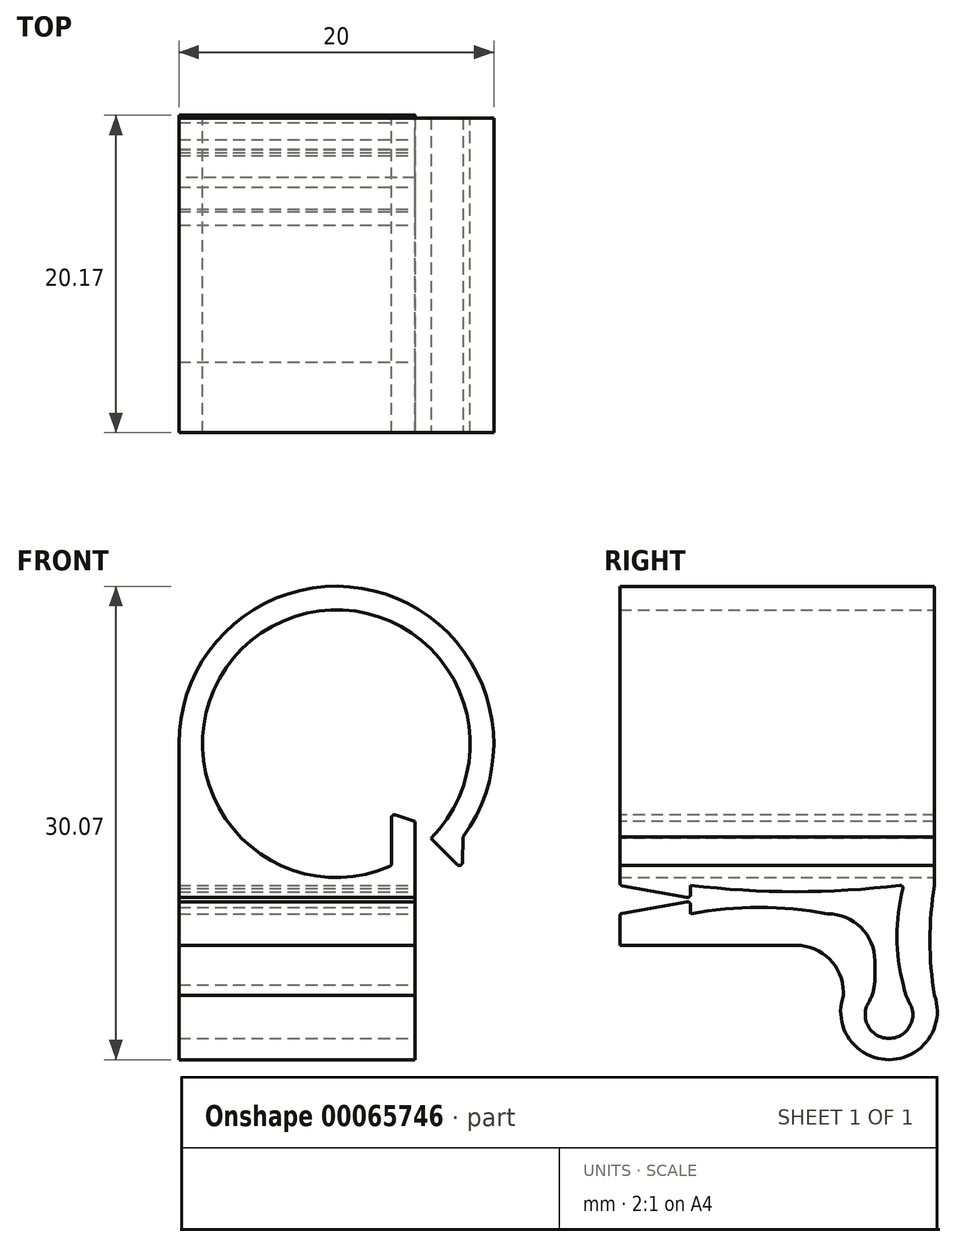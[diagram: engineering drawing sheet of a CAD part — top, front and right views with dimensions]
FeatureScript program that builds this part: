
annotation { "Feature Type Name" : "Feature", "Feature Type Description" : "" }
export const myFeature = defineFeature(function(context is Context, id is Id, definition is map)
    precondition{}
    {
        {
            var Q0;
            Q0=qCreatedBy(makeId("Front.planeOp"),FACE);
            var sketch = newSketch(context, id + "F0", { "sketchPlane" : qUnion([Q0])});
            skLineSegment(sketch, "E0", {"start": v(0, 0) * mm, "end": v(0, 18) * mm});
            skLineSegment(sketch, "E1", {"start": v(0, 0) * mm, "end": v(15, 0) * mm});
            skLineSegment(sketch, "E2", {"start": v(15, 0) * mm, "end": v(15, 18) * mm, "construction": true});
            skPoint(sketch, "E3", {"position": v(10, 18) * mm});
            skArc(sketch, "E4", {"start": v(0, 18) * mm, "mid": v(15, 26.66) * mm, "end": v(15, 9.34) * mm});
            skLineSegment(sketch, "E5", {"start": v(15, 9.34) * mm, "end": v(15, 0) * mm});
            skCircle(sketch, "E6", {"center": v(10, 18) * mm, "radius": 8.5 * mm});
            skSolve(sketch);
        }
        {
            var Q0;
            Q0=makeQuery(id+"F0.imprint","IMPRINT",FACE,{"disambiguationData":[TD([[makeQuery(id+"F0.imprint","IMPRINT",EDGE,{"derivedFrom":sQuery(id+"F0.wireOp",EDGE,"E0")}),-1.0]])]});
            extrude(context, id + "F1", {"entities" : qUnion([Q0]), "depth" : 20 * mm});
        }
        {
            var Q0;
            Q0=makeQuery(id+"F1.opExtrude","SWEPT_FACE",FACE,{"disambiguationData":[OSD([sQuery(id+"F0.wireOp",EDGE,"E5")])]});
            var sketch = newSketch(context, id + "F2", { "sketchPlane" : qUnion([Q0])});
            skLineSegment(sketch, "E7", {"start": v(-2, 2) * mm, "end": v(-2, 9) * mm});
            skLineSegment(sketch, "E8", {"start": v(-2, 9) * mm, "end": v(-20, 9) * mm});
            skLineSegment(sketch, "E9", {"start": v(-2, 2) * mm, "end": v(-3.8, 2) * mm});
            skLineSegment(sketch, "E10", {"start": v(-3.8, 2) * mm, "end": v(-3.8, 7.2) * mm});
            skLineSegment(sketch, "E11", {"start": v(-3.8, 7.2) * mm, "end": v(-20, 7.2) * mm});
            skLineSegment(sketch, "E12", {"start": v(-20, 9) * mm, "end": v(-20, 7.2) * mm});
            skLineSegment(sketch, "E13.bottom", {"start": v(-20, 0) * mm, "end": v(-5.8, 0) * mm});
            skLineSegment(sketch, "E13.top", {"start": v(-20, 5.2) * mm, "end": v(-5.8, 5.2) * mm});
            skLineSegment(sketch, "E13.left", {"start": v(-20, 0) * mm, "end": v(-20, 5.2) * mm});
            skLineSegment(sketch, "E13.right", {"start": v(-5.8, 0) * mm, "end": v(-5.8, 5.2) * mm});
            skSolve(sketch);
        }
        {
            var Q0;
            Q0 = qSketchRegion(id + "F2", true);
            extrude(context, id + "F3", {"entities" : qUnion([Q0]), "operationType" : NewBodyOperationType.REMOVE, "endBound" : BoundingType.THROUGH_ALL, "oppositeDirection" : true, "depth" : 25 * mm});
        }
        {
            var Q0;
            Q0=makeQuery(id+"F1.opExtrude","SWEPT_FACE",FACE,{"disambiguationData":[OSD([sQuery(id+"F0.wireOp",EDGE,"E5")])]});
            var sketch = newSketch(context, id + "F4", { "sketchPlane" : qUnion([Q0])});
            skLineSegment(sketch, "E14", {"start": v(-15.5, 7.2) * mm, "end": v(-15.5, 8) * mm});
            skLineSegment(sketch, "E15", {"start": v(-15.5, 8) * mm, "end": v(-20, 7.2) * mm});
            skLineSegment(sketch, "E16", {"start": v(-20, 7.2) * mm, "end": v(-15.5, 7.2) * mm});
            skLineSegment(sketch, "E17", {"start": v(-15.5, 9) * mm, "end": v(-15.5, 8.2) * mm});
            skLineSegment(sketch, "E18", {"start": v(-15.5, 8.2) * mm, "end": v(-20, 9) * mm});
            skLineSegment(sketch, "E19", {"start": v(-20, 9) * mm, "end": v(-15.5, 9) * mm});
            skSolve(sketch);
        }
        {
            var Q0;
            Q0 = qSketchRegion(id + "F4", true);
            var Q1;
            Q1=makeQuery(id+"F1.opExtrude","SWEPT_FACE",FACE,{"disambiguationData":[OSD([sQuery(id+"F0.wireOp",EDGE,"E0")])]});
            extrude(context, id + "F5", {"entities" : qUnion([Q0]), "operationType" : NewBodyOperationType.ADD, "endBound" : BoundingType.UP_TO_SURFACE, "oppositeDirection" : true, "endBoundEntityFace" : qUnion([Q1]), "depth" : 25 * mm});
        }
        {
            var Q0;
            {var subQ0=sQuery(id+"F0.wireOp",EDGE,"E6");var subQ1=sQuery(id+"F0.wireOp",EDGE,"E5");var subQ2=sQuery(id+"F0.wireOp",EDGE,"E4");var subQ3=sQuery(id+"F0.wireOp",EDGE,"E0");Q0=makeQuery(id+"F3.boolean.opBoolean","SPLIT",FACE,{"disambiguationData":[TD([makeQuery(id+"F1.opExtrude","SWEPT_FACE",FACE,{"disambiguationData":[OSD([subQ2])]})])],"derivedFrom":makeQuery(id+"F1.opExtrude","CAP_FACE",FACE,{"disambiguationData":[OSD([subQ3,sQuery(id+"F0.wireOp",EDGE,"E1"),subQ2,subQ1,subQ0])],"isStart":false})});}
            var sketch = newSketch(context, id + "F6", { "sketchPlane" : qUnion([Q0])});
            skLineSegment(sketch, "E20.bottom", {"start": v(15, 9.34) * mm, "end": v(16, 9.34) * mm});
            skLineSegment(sketch, "E20.top", {"start": v(15, 11.98) * mm, "end": v(16, 11.98) * mm});
            skLineSegment(sketch, "E20.left", {"start": v(15, 9.34) * mm, "end": v(15, 11.98) * mm});
            skLineSegment(sketch, "E20.right", {"start": v(16, 9.34) * mm, "end": v(16, 11.98) * mm});
            skSolve(sketch);
        }
        {
            var Q0;
            Q0 = qSketchRegion(id + "F6", true);
            extrude(context, id + "F7", {"entities" : qUnion([Q0]), "operationType" : NewBodyOperationType.REMOVE, "endBound" : BoundingType.THROUGH_ALL, "oppositeDirection" : true, "depth" : 25 * mm});
        }
        {
            var Q0;
            {var subQ0=sQuery(id+"F0.wireOp",EDGE,"E6");var subQ1=sQuery(id+"F0.wireOp",EDGE,"E5");var subQ2=sQuery(id+"F0.wireOp",EDGE,"E4");var subQ3=sQuery(id+"F0.wireOp",EDGE,"E0");Q0=makeQuery(id+"F3.boolean.opBoolean","SPLIT",FACE,{"disambiguationData":[TD([makeQuery(id+"F1.opExtrude","SWEPT_FACE",FACE,{"disambiguationData":[OSD([subQ2])]})])],"derivedFrom":makeQuery(id+"F1.opExtrude","CAP_FACE",FACE,{"disambiguationData":[OSD([subQ3,sQuery(id+"F0.wireOp",EDGE,"E1"),subQ2,subQ1,subQ0])],"isStart":false})});}
            var sketch = newSketch(context, id + "F8", { "sketchPlane" : qUnion([Q0])});
            skLineSegment(sketch, "E21.bottom", {"start": v(15, 10.06) * mm, "end": v(13.5, 10.06) * mm});
            skLineSegment(sketch, "E21.top", {"start": v(15, 13.56) * mm, "end": v(13.5, 13.56) * mm});
            skLineSegment(sketch, "E21.left", {"start": v(15, 10.06) * mm, "end": v(15, 13.56) * mm});
            skLineSegment(sketch, "E21.right", {"start": v(13.5, 10.06) * mm, "end": v(13.5, 13.56) * mm});
            skLineSegment(sketch, "E22", {"start": v(16, 11.98) * mm, "end": v(18, 10) * mm});
            skLineSegment(sketch, "E23", {"start": v(18, 10) * mm, "end": v(18.05, 12.06) * mm});
            skLineSegment(sketch, "E24", {"start": v(18.05, 12.06) * mm, "end": v(16, 11.98) * mm});
            skSolve(sketch);
        }
        {
            var Q0;
            Q0 = qSketchRegion(id + "F8", true);
            var Q1;
            Q1=makeQuery(id+"F1.opExtrude","CAP_FACE",FACE,{"disambiguationData":[OSD([sQuery(id+"F0.wireOp",EDGE,"E0"),sQuery(id+"F0.wireOp",EDGE,"E1"),sQuery(id+"F0.wireOp",EDGE,"E4"),sQuery(id+"F0.wireOp",EDGE,"E5"),sQuery(id+"F0.wireOp",EDGE,"E6")])],"isStart":true});
            extrude(context, id + "F9", {"entities" : qUnion([Q0]), "operationType" : NewBodyOperationType.ADD, "endBound" : BoundingType.UP_TO_SURFACE, "oppositeDirection" : true, "endBoundEntityFace" : qUnion([Q1]), "depth" : 25 * mm});
        }
        {
            var Q0;
            {var subQ0=sQuery(id+"F0.wireOp",EDGE,"E6");var subQ1=sQuery(id+"F0.wireOp",EDGE,"E5");var subQ2=sQuery(id+"F0.wireOp",EDGE,"E4");var subQ3=sQuery(id+"F0.wireOp",EDGE,"E0");Q0=makeQuery(id+"F9.boolean.opBoolean","MERGE",FACE,{"derivedFrom":[makeQuery(id+"F3.boolean.opBoolean","SPLIT",FACE,{"disambiguationData":[TD([makeQuery(id+"F1.opExtrude","SWEPT_FACE",FACE,{"disambiguationData":[OSD([subQ2])]})])],"derivedFrom":makeQuery(id+"F1.opExtrude","CAP_FACE",FACE,{"disambiguationData":[OSD([subQ3,sQuery(id+"F0.wireOp",EDGE,"E1"),subQ2,subQ1,subQ0])],"isStart":false})}),makeQuery(id+"F9.opExtrude","CAP_FACE",FACE,{"disambiguationData":[OSD([sQuery(id+"F8.wireOp",EDGE,"E21.bottom"),sQuery(id+"F8.wireOp",EDGE,"E21.top"),sQuery(id+"F8.wireOp",EDGE,"E21.left"),sQuery(id+"F8.wireOp",EDGE,"E21.right")])],"isStart":true}),makeQuery(id+"F9.opExtrude","CAP_FACE",FACE,{"disambiguationData":[OSD([sQuery(id+"F8.wireOp",EDGE,"E22"),sQuery(id+"F8.wireOp",EDGE,"E23"),sQuery(id+"F8.wireOp",EDGE,"E24")])],"isStart":true})]});}
            var sketch = newSketch(context, id + "F10", { "sketchPlane" : qUnion([Q0])});
            skLineSegment(sketch, "E25", {"start": v(16, 10) * mm, "end": v(16, 11.98) * mm});
            skLineSegment(sketch, "E26", {"start": v(17.07, 10.92) * mm, "end": v(16, 11.98) * mm});
            skLineSegment(sketch, "E27", {"start": v(13.5, 13.56) * mm, "end": v(15, 13.06) * mm});
            skLineSegment(sketch, "E28", {"start": v(15, 13.06) * mm, "end": v(15, 13.56) * mm});
            skLineSegment(sketch, "E29", {"start": v(15, 13.56) * mm, "end": v(13.5, 13.56) * mm});
            skLineSegment(sketch, "E30", {"start": v(16, 10) * mm, "end": v(17.07, 10) * mm});
            skLineSegment(sketch, "E31", {"start": v(17.07, 10) * mm, "end": v(17.07, 10.92) * mm});
            skSolve(sketch);
        }
        {
            var Q0;
            Q0 = qSketchRegion(id + "F10", true);
            var Q1;
            Q1=makeQuery(id+"F9.boolean.opBoolean","MERGE",FACE,{"derivedFrom":[makeQuery(id+"F1.opExtrude","CAP_FACE",FACE,{"disambiguationData":[OSD([sQuery(id+"F0.wireOp",EDGE,"E0"),sQuery(id+"F0.wireOp",EDGE,"E1"),sQuery(id+"F0.wireOp",EDGE,"E4"),sQuery(id+"F0.wireOp",EDGE,"E5"),sQuery(id+"F0.wireOp",EDGE,"E6")])],"isStart":true}),makeQuery(id+"F9.opExtrude","CAP_FACE",FACE,{"disambiguationData":[OSD([sQuery(id+"F8.wireOp",EDGE,"E21.bottom"),sQuery(id+"F8.wireOp",EDGE,"E21.top"),sQuery(id+"F8.wireOp",EDGE,"E21.left"),sQuery(id+"F8.wireOp",EDGE,"E21.right")])],"isStart":false}),makeQuery(id+"F9.opExtrude","CAP_FACE",FACE,{"disambiguationData":[OSD([sQuery(id+"F8.wireOp",EDGE,"E22"),sQuery(id+"F8.wireOp",EDGE,"E23"),sQuery(id+"F8.wireOp",EDGE,"E24")])],"isStart":false})]});
            extrude(context, id + "F11", {"entities" : qUnion([Q0]), "operationType" : NewBodyOperationType.REMOVE, "endBound" : BoundingType.UP_TO_SURFACE, "oppositeDirection" : true, "endBoundEntityFace" : qUnion([Q1]), "depth" : 25 * mm});
        }
        {
            var Q0;
            Q0=makeQuery(id+"F9.boolean.opBoolean","MERGE",FACE,{"derivedFrom":[makeQuery(id+"F7.boolean.opBoolean","MERGE",FACE,{"derivedFrom":[makeQuery(id+"F5.boolean.opBoolean","MERGE",FACE,{"derivedFrom":[makeQuery(id+"F1.opExtrude","SWEPT_FACE",FACE,{"disambiguationData":[OSD([sQuery(id+"F0.wireOp",EDGE,"E5")])]}),makeQuery(id+"F5.opExtrude","CAP_FACE",FACE,{"disambiguationData":[OSD([sQuery(id+"F4.wireOp",EDGE,"E14"),sQuery(id+"F4.wireOp",EDGE,"E15"),sQuery(id+"F4.wireOp",EDGE,"E16")])],"isStart":true}),makeQuery(id+"F5.opExtrude","CAP_FACE",FACE,{"disambiguationData":[OSD([sQuery(id+"F4.wireOp",EDGE,"E17"),sQuery(id+"F4.wireOp",EDGE,"E18"),sQuery(id+"F4.wireOp",EDGE,"E19")])],"isStart":true})]}),makeQuery(id+"F7.opExtrude","SWEPT_FACE",FACE,{"disambiguationData":[OSD([sQuery(id+"F6.wireOp",EDGE,"E20.left")])]})]}),makeQuery(id+"F9.opExtrude","SWEPT_FACE",FACE,{"disambiguationData":[OSD([sQuery(id+"F8.wireOp",EDGE,"E21.left")])]})]});
            var sketch = newSketch(context, id + "F12", { "sketchPlane" : qUnion([Q0])});
            skArc(sketch, "E32", {"start": v(-5.8, 2) * mm, "mid": v(-2.9, -2.07) * mm, "end": v(0, 2) * mm});
            skLineSegment(sketch, "E33", {"start": v(-5.8, 2) * mm, "end": v(0, 2) * mm});
            skSolve(sketch);
        }
        {
            var Q0;
            Q0 = qSketchRegion(id + "F12", true);
            var Q1;
            Q1=makeQuery(id+"F5.boolean.opBoolean","MERGE",FACE,{"derivedFrom":[makeQuery(id+"F1.opExtrude","SWEPT_FACE",FACE,{"disambiguationData":[OSD([sQuery(id+"F0.wireOp",EDGE,"E0")])]}),makeQuery(id+"F5.opExtrude","CAP_FACE",FACE,{"disambiguationData":[OSD([sQuery(id+"F4.wireOp",EDGE,"E14"),sQuery(id+"F4.wireOp",EDGE,"E15"),sQuery(id+"F4.wireOp",EDGE,"E16")])],"isStart":false}),makeQuery(id+"F5.opExtrude","CAP_FACE",FACE,{"disambiguationData":[OSD([sQuery(id+"F4.wireOp",EDGE,"E17"),sQuery(id+"F4.wireOp",EDGE,"E18"),sQuery(id+"F4.wireOp",EDGE,"E19")])],"isStart":false})]});
            extrude(context, id + "F13", {"entities" : qUnion([Q0]), "operationType" : NewBodyOperationType.ADD, "endBound" : BoundingType.UP_TO_SURFACE, "oppositeDirection" : true, "endBoundEntityFace" : qUnion([Q1]), "depth" : 25 * mm});
        }
        {
            var Q0;
            Q0=makeQuery(id+"F13.boolean.opBoolean","MERGE",FACE,{"derivedFrom":[makeQuery(id+"F9.boolean.opBoolean","MERGE",FACE,{"derivedFrom":[makeQuery(id+"F7.boolean.opBoolean","MERGE",FACE,{"derivedFrom":[makeQuery(id+"F5.boolean.opBoolean","MERGE",FACE,{"derivedFrom":[makeQuery(id+"F1.opExtrude","SWEPT_FACE",FACE,{"disambiguationData":[OSD([sQuery(id+"F0.wireOp",EDGE,"E5")])]}),makeQuery(id+"F5.opExtrude","CAP_FACE",FACE,{"disambiguationData":[OSD([sQuery(id+"F4.wireOp",EDGE,"E14"),sQuery(id+"F4.wireOp",EDGE,"E15"),sQuery(id+"F4.wireOp",EDGE,"E16")])],"isStart":true}),makeQuery(id+"F5.opExtrude","CAP_FACE",FACE,{"disambiguationData":[OSD([sQuery(id+"F4.wireOp",EDGE,"E17"),sQuery(id+"F4.wireOp",EDGE,"E18"),sQuery(id+"F4.wireOp",EDGE,"E19")])],"isStart":true})]}),makeQuery(id+"F7.opExtrude","SWEPT_FACE",FACE,{"disambiguationData":[OSD([sQuery(id+"F6.wireOp",EDGE,"E20.left")])]})]}),makeQuery(id+"F9.opExtrude","SWEPT_FACE",FACE,{"disambiguationData":[OSD([sQuery(id+"F8.wireOp",EDGE,"E21.left")])]})]}),makeQuery(id+"F13.opExtrude","CAP_FACE",FACE,{"disambiguationData":[OSD([sQuery(id+"F12.wireOp",EDGE,"E32"),sQuery(id+"F12.wireOp",EDGE,"E33")])],"isStart":true})]});
            var sketch = newSketch(context, id + "F14", { "sketchPlane" : qUnion([Q0])});
            skArc(sketch, "E34", {"start": v(-3.8, 2) * mm, "mid": v(-2.9, -0.72) * mm, "end": v(-2, 2) * mm});
            skLineSegment(sketch, "E35", {"start": v(-3.8, 2) * mm, "end": v(-2, 2) * mm});
            skArc(sketch, "E36", {"start": v(0, 9) * mm, "mid": v(-0.3, 5.5) * mm, "end": v(0, 2) * mm});
            skLineSegment(sketch, "E37", {"start": v(0, 2) * mm, "end": v(0, 9) * mm});
            skSolve(sketch);
        }
        {
            var Q0;
            Q0 = qSketchRegion(id + "F14", true);
            extrude(context, id + "F15", {"entities" : qUnion([Q0]), "operationType" : NewBodyOperationType.REMOVE, "endBound" : BoundingType.THROUGH_ALL, "oppositeDirection" : true, "depth" : 25 * mm});
        }
        {
            var Q0;
            Q0=makeQuery(id+"F3.boolean.opBoolean","COPY",EDGE,{"derivedFrom":makeQuery(id+"F3.opExtrude","SWEPT_EDGE",EDGE,{"disambiguationData":[OSD([sQuery(id+"F2.wireOp",EDGE,"E10"),sQuery(id+"F2.wireOp",EDGE,"E11")])]})});
            var Q1;
            Q1=makeQuery(id+"F3.boolean.opBoolean","COPY",EDGE,{"derivedFrom":makeQuery(id+"F3.opExtrude","SWEPT_EDGE",EDGE,{"disambiguationData":[OSD([sQuery(id+"F2.wireOp",EDGE,"E13.top"),sQuery(id+"F2.wireOp",EDGE,"E13.right")])]})});
            var Q2;
            {var subQ0=sQuery(id+"F2.wireOp",EDGE,"E10");Q2=makeQuery(id+"F15.boolean.opBoolean","MERGE",EDGE,{"derivedFrom":[makeQuery(id+"F3.boolean.opBoolean","COPY",EDGE,{"derivedFrom":makeQuery(id+"F3.opExtrude","SWEPT_EDGE",EDGE,{"disambiguationData":[OSD([sQuery(id+"F2.wireOp",EDGE,"E9"),subQ0])]})}),makeQuery(id+"F15.opExtrude","SWEPT_EDGE",EDGE,{"disambiguationData":[OSD([subQ0,sQuery(id+"F14.wireOp",EDGE,"E34"),sQuery(id+"F14.wireOp",EDGE,"E35")])]})]});}
            var Q3;
            {var subQ0=sQuery(id+"F2.wireOp",EDGE,"E7");Q3=makeQuery(id+"F15.boolean.opBoolean","MERGE",EDGE,{"derivedFrom":[makeQuery(id+"F3.boolean.opBoolean","COPY",EDGE,{"derivedFrom":makeQuery(id+"F3.opExtrude","SWEPT_EDGE",EDGE,{"disambiguationData":[OSD([subQ0,sQuery(id+"F2.wireOp",EDGE,"E9")])]})}),makeQuery(id+"F15.opExtrude","SWEPT_EDGE",EDGE,{"disambiguationData":[OSD([subQ0,sQuery(id+"F14.wireOp",EDGE,"E34"),sQuery(id+"F14.wireOp",EDGE,"E35")])]})]});}
            var Q4;
            Q4=makeQuery(id+"F15.boolean.opBoolean","COPY",EDGE,{"derivedFrom":makeQuery(id+"F15.opExtrude","SWEPT_EDGE",EDGE,{"disambiguationData":[OSD([sQuery(id+"F0.wireOp",EDGE,"E0"),sQuery(id+"F0.wireOp",EDGE,"E1"),sQuery(id+"F0.wireOp",EDGE,"E4"),sQuery(id+"F0.wireOp",EDGE,"E5"),sQuery(id+"F0.wireOp",EDGE,"E6"),sQuery(id+"F6.wireOp",EDGE,"E20.left"),sQuery(id+"F8.wireOp",EDGE,"E21.left"),sQuery(id+"F14.wireOp",EDGE,"E36"),sQuery(id+"F14.wireOp",EDGE,"E37")])]})});
            var Q5;
            {var subQ0=sQuery(id+"F12.wireOp",EDGE,"E32");Q5=makeQuery(id+"F15.boolean.opBoolean","MERGE",EDGE,{"derivedFrom":[makeQuery(id+"F13.opExtrude","SWEPT_EDGE",EDGE,{"disambiguationData":[OSD([sQuery(id+"F0.wireOp",EDGE,"E0"),sQuery(id+"F0.wireOp",EDGE,"E1"),sQuery(id+"F0.wireOp",EDGE,"E4"),sQuery(id+"F0.wireOp",EDGE,"E5"),sQuery(id+"F0.wireOp",EDGE,"E6"),sQuery(id+"F6.wireOp",EDGE,"E20.left"),sQuery(id+"F8.wireOp",EDGE,"E21.left"),subQ0,sQuery(id+"F12.wireOp",EDGE,"E33")])]}),makeQuery(id+"F15.opExtrude","SWEPT_EDGE",EDGE,{"disambiguationData":[OSD([subQ0,sQuery(id+"F14.wireOp",EDGE,"E36"),sQuery(id+"F14.wireOp",EDGE,"E37")])]})]});}
            fillet(context, id + "F16", {"entities" : qUnion([Q0, Q1, Q2, Q3, Q4, Q5]), "radius" : 3 * mm, "tangentPropagation" : true, "allowEdgeOverflow" : false});
        }
        {
            var Q0;
            {var subQ0=sQuery(id+"F0.wireOp",EDGE,"E5");Q0=makeQuery(id+"F5.boolean.opBoolean","MERGE",EDGE,{"derivedFrom":[makeQuery(id+"F3.boolean.opBoolean","COPY",EDGE,{"derivedFrom":makeQuery(id+"F3.opExtrude","SWEPT_EDGE",EDGE,{"disambiguationData":[OSD([subQ0,sQuery(id+"F2.wireOp",EDGE,"E11"),sQuery(id+"F2.wireOp",EDGE,"E12")])]})}),makeQuery(id+"F5.opExtrude","SWEPT_EDGE",EDGE,{"disambiguationData":[OSD([subQ0,sQuery(id+"F4.wireOp",EDGE,"E15"),sQuery(id+"F4.wireOp",EDGE,"E16")])]})]});}
            var Q1;
            {var subQ0=sQuery(id+"F0.wireOp",EDGE,"E5");Q1=makeQuery(id+"F5.boolean.opBoolean","MERGE",EDGE,{"derivedFrom":[makeQuery(id+"F3.boolean.opBoolean","COPY",EDGE,{"derivedFrom":makeQuery(id+"F3.opExtrude","SWEPT_EDGE",EDGE,{"disambiguationData":[OSD([subQ0,sQuery(id+"F2.wireOp",EDGE,"E8"),sQuery(id+"F2.wireOp",EDGE,"E12")])]})}),makeQuery(id+"F5.opExtrude","SWEPT_EDGE",EDGE,{"disambiguationData":[OSD([subQ0,sQuery(id+"F4.wireOp",EDGE,"E18"),sQuery(id+"F4.wireOp",EDGE,"E19")])]})]});}
            var Q2;
            Q2=makeQuery(id+"F5.opExtrude","SWEPT_EDGE",EDGE,{"disambiguationData":[OSD([sQuery(id+"F4.wireOp",EDGE,"E17"),sQuery(id+"F4.wireOp",EDGE,"E18")])]});
            var Q3;
            Q3=makeQuery(id+"F5.opExtrude","SWEPT_EDGE",EDGE,{"disambiguationData":[OSD([sQuery(id+"F4.wireOp",EDGE,"E14"),sQuery(id+"F4.wireOp",EDGE,"E15")])]});
            var Q4;
            Q4=makeQuery(id+"F3.boolean.opBoolean","COPY",EDGE,{"derivedFrom":makeQuery(id+"F3.opExtrude","SWEPT_EDGE",EDGE,{"disambiguationData":[OSD([sQuery(id+"F2.wireOp",EDGE,"E7"),sQuery(id+"F2.wireOp",EDGE,"E8")])]})});
            var Q5;
            Q5=makeQuery(id+"F9.opExtrude","SWEPT_EDGE",EDGE,{"disambiguationData":[OSD([sQuery(id+"F8.wireOp",EDGE,"E22"),sQuery(id+"F8.wireOp",EDGE,"E23")])]});
            var Q6;
            {var subQ0=sQuery(id+"F0.wireOp",EDGE,"E6");Q6=makeQuery(id+"F11.boolean.opBoolean","MERGE",EDGE,{"derivedFrom":[makeQuery(id+"F7.boolean.opBoolean","COPY",EDGE,{"derivedFrom":makeQuery(id+"F7.opExtrude","SWEPT_EDGE",EDGE,{"disambiguationData":[OSD([subQ0,sQuery(id+"F6.wireOp",EDGE,"E20.top"),sQuery(id+"F6.wireOp",EDGE,"E20.right")])]})}),makeQuery(id+"F11.opExtrude","SWEPT_EDGE",EDGE,{"disambiguationData":[OSD([subQ0,sQuery(id+"F10.wireOp",EDGE,"E25"),sQuery(id+"F10.wireOp",EDGE,"E26")])]})]});}
            var Q7;
            {var subQ0=sQuery(id+"F8.wireOp",EDGE,"E21.right");Q7=makeQuery(id+"F11.boolean.opBoolean","MERGE",EDGE,{"derivedFrom":[makeQuery(id+"F9.opExtrude","SWEPT_EDGE",EDGE,{"disambiguationData":[OSD([sQuery(id+"F8.wireOp",EDGE,"E21.top"),subQ0])]}),makeQuery(id+"F11.opExtrude","SWEPT_EDGE",EDGE,{"disambiguationData":[OSD([subQ0,sQuery(id+"F10.wireOp",EDGE,"E27"),sQuery(id+"F10.wireOp",EDGE,"E29")])]})]});}
            var Q8;
            Q8=makeQuery(id+"F11.boolean.opBoolean","COPY",EDGE,{"derivedFrom":makeQuery(id+"F11.opExtrude","SWEPT_EDGE",EDGE,{"disambiguationData":[OSD([sQuery(id+"F0.wireOp",EDGE,"E5"),sQuery(id+"F6.wireOp",EDGE,"E20.left"),sQuery(id+"F8.wireOp",EDGE,"E21.left"),sQuery(id+"F10.wireOp",EDGE,"E27"),sQuery(id+"F10.wireOp",EDGE,"E28")])]})});
            var Q9;
            Q9=makeQuery(id+"F9.boolean.opBoolean","INTERSECT",EDGE,{"derivedFrom":[makeQuery(id+"F1.opExtrude","SWEPT_FACE",FACE,{"disambiguationData":[OSD([sQuery(id+"F0.wireOp",EDGE,"E6")])]}),makeQuery(id+"F9.opExtrude","SWEPT_FACE",FACE,{"disambiguationData":[OSD([sQuery(id+"F8.wireOp",EDGE,"E21.right")])]})]});
            fillet(context, id + "F17", {"entities" : qUnion([Q0, Q1, Q2, Q3, Q4, Q5, Q6, Q7, Q8, Q9]), "radius" : 0.2 * mm, "tangentPropagation" : true, "allowEdgeOverflow" : false});
        }
        {
            var Q0;
            Q0=makeQuery(id+"F13.boolean.opBoolean","MERGE",FACE,{"derivedFrom":[makeQuery(id+"F9.boolean.opBoolean","MERGE",FACE,{"derivedFrom":[makeQuery(id+"F7.boolean.opBoolean","MERGE",FACE,{"derivedFrom":[makeQuery(id+"F5.boolean.opBoolean","MERGE",FACE,{"derivedFrom":[makeQuery(id+"F1.opExtrude","SWEPT_FACE",FACE,{"disambiguationData":[OSD([sQuery(id+"F0.wireOp",EDGE,"E5")])]}),makeQuery(id+"F5.opExtrude","CAP_FACE",FACE,{"disambiguationData":[OSD([sQuery(id+"F4.wireOp",EDGE,"E14"),sQuery(id+"F4.wireOp",EDGE,"E15"),sQuery(id+"F4.wireOp",EDGE,"E16")])],"isStart":true}),makeQuery(id+"F5.opExtrude","CAP_FACE",FACE,{"disambiguationData":[OSD([sQuery(id+"F4.wireOp",EDGE,"E17"),sQuery(id+"F4.wireOp",EDGE,"E18"),sQuery(id+"F4.wireOp",EDGE,"E19")])],"isStart":true})]}),makeQuery(id+"F7.opExtrude","SWEPT_FACE",FACE,{"disambiguationData":[OSD([sQuery(id+"F6.wireOp",EDGE,"E20.left")])]})]}),makeQuery(id+"F9.opExtrude","SWEPT_FACE",FACE,{"disambiguationData":[OSD([sQuery(id+"F8.wireOp",EDGE,"E21.left")])]})]}),makeQuery(id+"F13.opExtrude","CAP_FACE",FACE,{"disambiguationData":[OSD([sQuery(id+"F12.wireOp",EDGE,"E32"),sQuery(id+"F12.wireOp",EDGE,"E33")])],"isStart":true})]});
            var sketch = newSketch(context, id + "F18", { "sketchPlane" : qUnion([Q0])});
            skArc(sketch, "E38", {"start": v(-15.5, 9) * mm, "mid": v(-8.85, 8.6) * mm, "end": v(-2.2, 9) * mm});
            skLineSegment(sketch, "E39", {"start": v(-15.5, 9) * mm, "end": v(-2.2, 9) * mm});
            skArc(sketch, "E40", {"start": v(-6.8, 7.2) * mm, "mid": v(-11.15, 7.6) * mm, "end": v(-15.5, 7.2) * mm});
            skLineSegment(sketch, "E41", {"start": v(-15.5, 7.2) * mm, "end": v(-6.8, 7.2) * mm});
            skArc(sketch, "E42", {"start": v(-2, 8.8) * mm, "mid": v(-2.38, 5.14) * mm, "end": v(-1.6, 1.55) * mm});
            skLineSegment(sketch, "E43", {"start": v(-1.6, 1.55) * mm, "end": v(-2, 8.8) * mm});
            skSolve(sketch);
        }
        {
            var Q0;
            Q0 = qSketchRegion(id + "F18", true);
            var Q1;
            Q1=makeQuery(id+"F13.boolean.opBoolean","MERGE",FACE,{"derivedFrom":[makeQuery(id+"F5.boolean.opBoolean","MERGE",FACE,{"derivedFrom":[makeQuery(id+"F1.opExtrude","SWEPT_FACE",FACE,{"disambiguationData":[OSD([sQuery(id+"F0.wireOp",EDGE,"E0")])]}),makeQuery(id+"F5.opExtrude","CAP_FACE",FACE,{"disambiguationData":[OSD([sQuery(id+"F4.wireOp",EDGE,"E14"),sQuery(id+"F4.wireOp",EDGE,"E15"),sQuery(id+"F4.wireOp",EDGE,"E16")])],"isStart":false}),makeQuery(id+"F5.opExtrude","CAP_FACE",FACE,{"disambiguationData":[OSD([sQuery(id+"F4.wireOp",EDGE,"E17"),sQuery(id+"F4.wireOp",EDGE,"E18"),sQuery(id+"F4.wireOp",EDGE,"E19")])],"isStart":false})]}),makeQuery(id+"F13.opExtrude","CAP_FACE",FACE,{"disambiguationData":[OSD([sQuery(id+"F12.wireOp",EDGE,"E32"),sQuery(id+"F12.wireOp",EDGE,"E33")])],"isStart":false})]});
            extrude(context, id + "F19", {"entities" : qUnion([Q0]), "operationType" : NewBodyOperationType.ADD, "endBound" : BoundingType.UP_TO_SURFACE, "oppositeDirection" : true, "endBoundEntityFace" : qUnion([Q1]), "depth" : 25 * mm});
        }
    });
